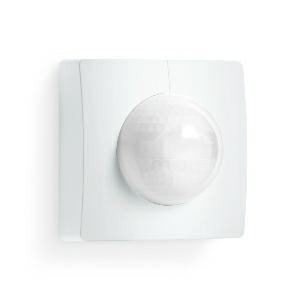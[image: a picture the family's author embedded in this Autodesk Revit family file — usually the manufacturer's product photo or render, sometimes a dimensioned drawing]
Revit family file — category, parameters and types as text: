
# Revit family: is_3180_010508
name_source: partatom
category: Elektroinstallationen
revit_build: Autodesk Revit 2016 (Build: 20190508_0715(x64)
units: mm (PartAtom-declared; Revit-internal decimal feet)

## family parameters
Basisbauteil = Fläche
Beim Laden mit Abzugskörper schneiden = Nein
Bemaßung runder Anschluss = Durchmesser verwenden
Beschriftungsausrichtung beibehalten = Nein
Gemeinsam genutzt = Nein
Raumberechnungspunkt = Nein
Teiletyp = Normal

## types (1)
- IS 3180
    Apparent Load = 0 VA
    Beschreibung = Type: Motion detectors; Dimensions (L x W x H): 65 x 95 x 95 mm; Mains power supply: 220 – 240 V / 50 – 60 Hz; Power consumption: 0,3 W; Sensor Technology: passive infrared; Application, place: Outdoors, Indoors; Application, room: corridor / aisle, function room / ancillary room, stairwell, multi-storey / underground car park, outdoors, all round the building, courtyard & driveway, Indoors; Installation site: wall, corner; Installation: Surface wiring; Switching zones: 448 switching zones; Electronic scalability: No; Mechanical scalability: No; Mounting height: 1,80 – 2,50 m; Optimum mounting height: 2 m; Detection angle: 180 °; Angle of aperture: 90 °; Sneak-by guard: Yes; Capability of masking out individual segments: Yes; Reach, radial: r = 3 m (14 m²) / r = 4 m (25 m²); Reach, tangential: r = 6 m (57 m²) / r = 20 m (628 m²); Twilight setting TEACH: Yes; Twilight setting: 2 – 1000 lx; Time setting: 5 sec – 15 min; Constant-lighting control: No; Basic light level function: No; Functions: Normal / test mode, Manual ON / ON-OFF; Settings via: Remote control, Potentiometers, Smart Remote; With remote control: No; Interconnection: Yes; Type of interconnection: Master/master; IP-rating: IP54; Material: Plastic; Ambient temperature: -20 – 50 °C; Colour: white; Colour, RAL: 9003; Manufacturer's Warranty: 5 years; Version: PF - surface, sq.; PU1, EAN: 4007841010508
    Height = 95 mm
    Hersteller = Steinel
    Length = 65 mm
    Maximum range = 22.153 m
    ModVariant = Nein
    Modell = 010508
    Mounting Type = Surface mounted
    Number of Poles = 1
    OnlyDefault = Ja
    Power Factor = 1
    Product Name = IS 3180
    Product group = Sensor-switched indoor light
    ProductGroupID = 30
    Protection Class = Protection class
    Protection Degree = IP 54
    RlxData = <blob elided: 167273 chars, md5=70717685>
    Sensor characteristics = Semi circular 145°-300°
    Sensor type = Passive (infrared)
    SensorDataFile = <blob elided: 5082 chars, md5=d953030a>
    Type of entry = Motion
    Typenbild = produkt1_010508.jpg
    Typenkommentare = Product without accessories
    URL = http://relux.com
    VarID = ---
    Voltage = 0 V
    Vorgabe-Ansicht = 1800 mm
    Weight = 0.00 kg
    Width = 95 mm

## geometry (parser evidence)
native form markers: Sweep x15
no freeform markers — native parametric forms only
